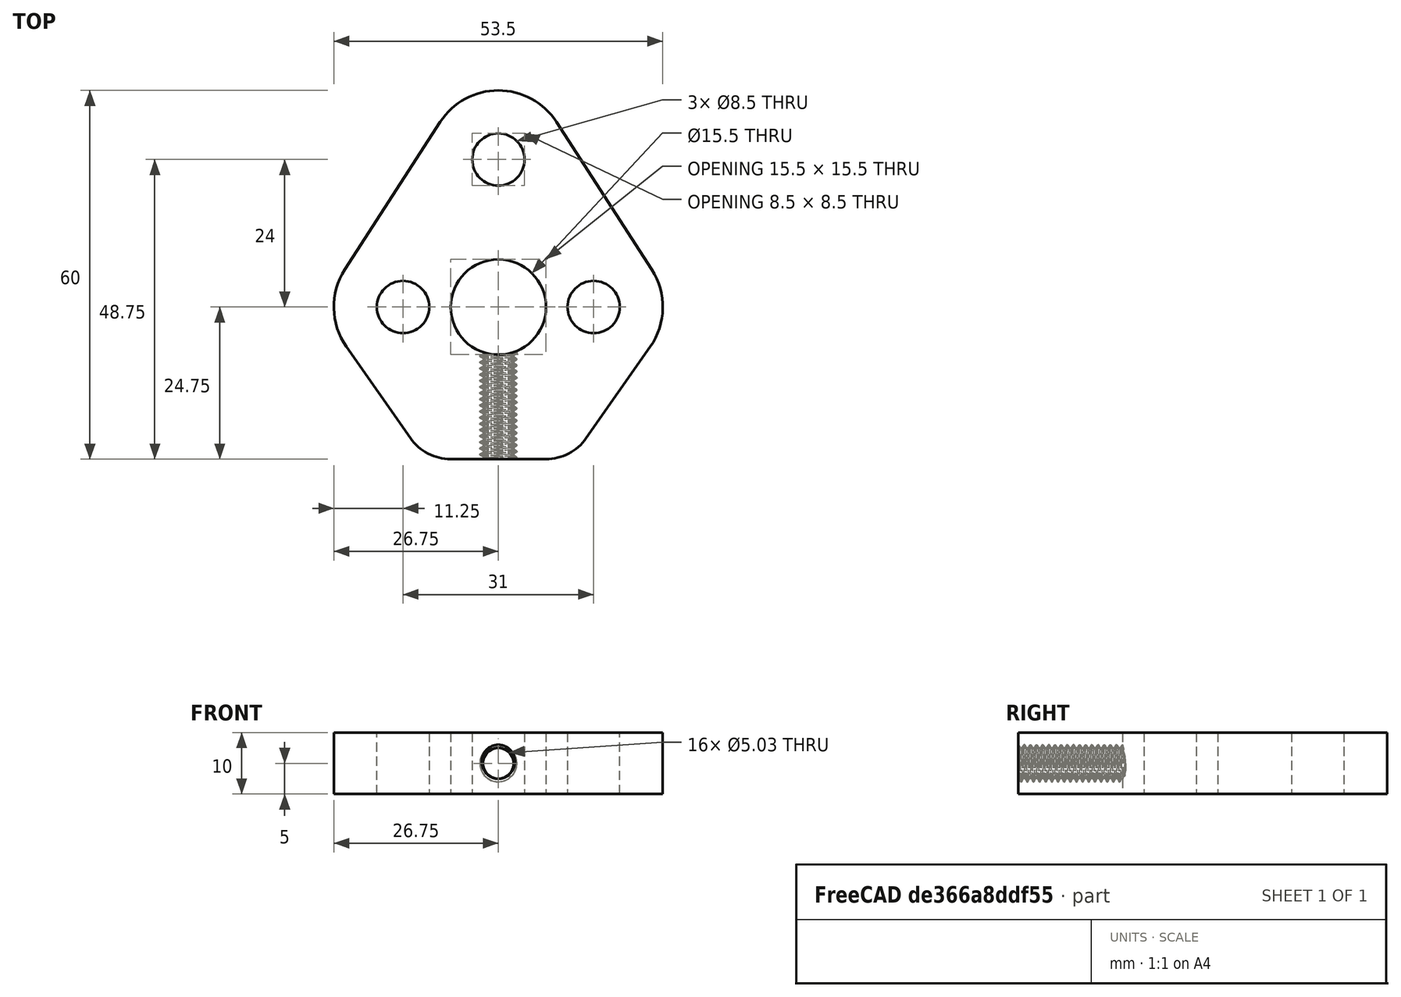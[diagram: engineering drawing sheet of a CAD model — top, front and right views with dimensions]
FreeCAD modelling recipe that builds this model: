
FCSTD DOCUMENT  (FreeCAD 0.20R29177 (Git))
Label: Поворот сортировщика семян
License: All rights reserved
LicenseURL: http://en.wikipedia.org/wiki/All_rights_reserved
objects: TechDraw::DrawProjGroupItem×4, Sketcher::SketchObject×2, TechDraw::DrawViewBalloon×2, TechDraw::DrawViewDimension×2, Mesh::Feature×1, PartDesign::Pad×1, PartDesign::Mirrored×1, TechDraw::DrawSVGTemplate×1, PartDesign::Hole×1, PartDesign::Body×1, TechDraw::DrawProjGroup×1, TechDraw::DrawPage×1
note: 8 computed .brp shape members not serialized (recipe doc carries the construction recipe); baked Part::Feature solids carry a one-line shape summary decoded from their .brp

FEATURE [Mesh::Feature] __________________________________________________2  label="поворот сортировщика семян2"
FEATURE [Sketcher::SketchObject] Sketch
  FullyConstrained = true
  MapMode = 5
  Support = -> [XY_Plane]
  sketch-geometry (12):
    g0: Circle CenterX=15.5 CenterY=0 CenterZ=0 NormalX=0 NormalY=0 NormalZ=1 AngleXU=0 Radius=4.25
    g1: ArcOfCircle CenterX=0 CenterY=0 CenterZ=0 NormalX=0 NormalY=0 NormalZ=1 AngleXU=0 Radius=7.75 StartAngle=4.71239 EndAngle=7.85398
    g2: ArcOfCircle CenterX=0 CenterY=24 CenterZ=0 NormalX=0 NormalY=0 NormalZ=1 AngleXU=0 Radius=4.25 StartAngle=4.71239 EndAngle=7.85398
    g3: ArcOfCircle CenterX=0 CenterY=24 CenterZ=0 NormalX=0 NormalY=0 NormalZ=1 AngleXU=0 Radius=11.25 StartAngle=0.573441 EndAngle=1.5708
    g4: ArcOfCircle CenterX=15.5 CenterY=0 CenterZ=0 NormalX=0 NormalY=0 NormalZ=1 AngleXU=0 Radius=11.25 StartAngle=5.67281 EndAngle=6.85663
    g5: ArcOfCircle CenterX=7.75 CenterY=-16.75 CenterZ=0 NormalX=0 NormalY=0 NormalZ=1 AngleXU=0 Radius=8 StartAngle=4.71239 EndAngle=5.67281
    g6: LineSegment StartX=7.75 StartY=-24.75 StartZ=0 EndX=0 EndY=-24.75 EndZ=0
    g7: LineSegment StartX=14.3055 StartY=-21.3354 StartZ=0 EndX=24.7187 EndY=-6.44818 EndZ=0
    g8: LineSegment StartX=0 StartY=-24.75 StartZ=0 EndX=-1.4e-15 EndY=-7.75 EndZ=0
    g9: LineSegment StartX=2.4e-15 StartY=7.75 StartZ=0 EndX=-8e-16 EndY=19.75 EndZ=0
    g10: LineSegment StartX=1.3e-15 StartY=28.25 StartZ=0 EndX=7e-16 EndY=35.25 EndZ=0
    g11: LineSegment StartX=9.45044 StartY=30.1034 StartZ=0 EndX=24.9504 EndY=6.10341 EndZ=0
  constraints (38):
    c: PointOnObject(g0,g-1)
    c: Coincident(g1,g-1)
    c: PointOnObject(g1,g-2)
    c: PointOnObject(g1,g-2)
    c: PointOnObject(g2,g-2)
    c: PointOnObject(g2,g-2)
    c: PointOnObject(g2,g-2)
    c: Coincident(g3,g2)
    c: PointOnObject(g3,g-2)
    c: Coincident(g4,g0)
    c: Coincident(g6,g5)
    c: PointOnObject(g6,g-2)
    c: Horizontal(g6)
    c: Coincident(g7,g5)
    c: Coincident(g7,g4)
    c: Coincident(g8,g6)
    c: Coincident(g8,g1)
    c: Coincident(g9,g1)
    c: Coincident(g9,g2)
    c: Coincident(g10,g2)
    c: Coincident(g10,g3)
    c: Coincident(g11,g3)
    c: Coincident(g11,g4)
    c: Diameter(g0) = 8.5
    c: Diameter(g2) = 8.5
    c: Diameter(g1) = 15.5
    c: DistanceX(g0) = 15.5
    c: DistanceY(g2) = 24
    c: Diameter(g4) = 22.5
    c: Equal(g3,g4)
    c: Tangent(g4,g11)
    c: Tangent(g11,g3)
    c: Tangent(g4,g7)
    c: Tangent(g6,g5)
    c: Tangent(g5,g7)
    c: Distance(g8) = 17
    c: Diameter(g5) = 16
    c: DistanceX(g5) = 7.75
FEATURE [PartDesign::Pad] Pad
  Direction = (0,0,1)
  Length = 10
  Length2 = 100
  Midplane = true
  Profile = -> Sketch
  Type = 0
FEATURE [PartDesign::Mirrored] Mirrored
  BaseFeature = -> Pad
  MirrorPlane = -> Sketch [V_Axis]
  Originals = -> [Pad]
FEATURE [TechDraw::DrawSVGTemplate] Template
  EditableTexts = AUTHOR_NAME=AUTHOR NAME; DN=DN; DRAWING_TITLE=DRAWING TITLE; FC-DATE=DD/MM/YYYY; FC-REV=REV A; FC-SC=SCALE; FC-SH=X / Y; FC-SI=A4; FreeCAD_DRAWING=FreeCAD DRAWING; PN=PN
  Height = 210
  Orientation = 1
  Width = 297
FEATURE [Sketcher::SketchObject] Sketch001
  FullyConstrained = true
  MapMode = 5
  Placement = pos=(0,0,0) rot=(1,0,0;1.5708rad)
  Support = -> [XZ_Plane]
  sketch-geometry (1):
    g0: Circle CenterX=0 CenterY=0 CenterZ=0 NormalX=0 NormalY=0 NormalZ=1 AngleXU=0 Radius=3
  constraints (2):
    c: Coincident(g0,g-1)
    c: Diameter(g0) = 6
FEATURE [PartDesign::Hole] Hole
  BaseFeature = -> Mirrored
  CustomThreadClearance = 0
  Depth = 163.486
  DepthType = 1
  Diameter = 5.026
  DrillForDepth = false
  DrillPoint = 1
  DrillPointAngle = 118
  HoleCutCountersinkAngle = 90
  HoleCutCustomValues = false
  HoleCutDepth = 6.4
  HoleCutDiameter = 13.4
  HoleCutType = 2
  ModelThread = true
  Profile = -> Sketch001
  Refine = true
  Reversed = true
  Tapered = false
  TaperedAngle = 90
  ThreadClass = 0
  ThreadDepth = 163.486
  ThreadDepthType = 0
  ThreadDirection = 0
  ThreadFit = 0
  ThreadSize = 14
  ThreadType = 1
  Threaded = true
  UseCustomThreadClearance = false
FEATURE [PartDesign::Body] Body
  Group = -> [Sketch,Pad,Mirrored,Sketch001,Hole]
  Origin = -> Origin
  Tip = -> Hole
FEATURE [TechDraw::DrawProjGroupItem] ProjItem  label="Front"
  CoarseView = false
  Direction = (0,0,-1)
  Focus = 100
  HardHidden = false
  IsoCount = 0
  IsoHidden = false
  IsoVisible = false
  LockPosition = true
  Perspective = false
  Rotation = 0
  RotationVector = (1,0,0)
  ScaleType = 2
  SeamHidden = false
  SeamVisible = true
  SmoothHidden = false
  SmoothVisible = true
  Source = -> [Body]
  Type = 0
  X = 0
  XDirection = (1,0,0)
  Y = 0
FEATURE [TechDraw::DrawProjGroupItem] ProjItem003  label="Top"
  CoarseView = false
  Direction = (0,-1,0)
  Focus = 100
  HardHidden = false
  IsoCount = 0
  IsoHidden = false
  IsoVisible = false
  LockPosition = false
  Perspective = false
  Rotation = 0
  RotationVector = (1,0,0)
  ScaleType = 2
  SeamHidden = false
  SeamVisible = true
  SmoothHidden = false
  SmoothVisible = true
  Source = -> [Body]
  Type = 4
  X = 0
  XDirection = (1,0,0)
  Y = -100
FEATURE [TechDraw::DrawProjGroupItem] ProjItem004  label="Left"
  CoarseView = false
  Direction = (-1,0,-1e-16)
  Focus = 100
  HardHidden = false
  IsoCount = 0
  IsoHidden = false
  IsoVisible = false
  LockPosition = false
  Perspective = false
  Rotation = 0
  RotationVector = (1,0,0)
  ScaleType = 2
  SeamHidden = false
  SeamVisible = true
  SmoothHidden = false
  SmoothVisible = true
  Source = -> [Body]
  Type = 1
  X = 50
  XDirection = (1e-16,0,-1)
  Y = 0
FEATURE [TechDraw::DrawProjGroupItem] ProjItem005  label="FrontTopLeft"
  CoarseView = false
  Direction = (-0.57735,-0.57735,-0.57735)
  Focus = 100
  HardHidden = false
  IsoCount = 0
  IsoHidden = false
  IsoVisible = false
  LockPosition = false
  Perspective = false
  Rotation = 0
  RotationVector = (1,0,0)
  ScaleType = 2
  SeamHidden = false
  SeamVisible = true
  SmoothHidden = false
  SmoothVisible = true
  Source = -> [Body]
  Type = 6
  X = 67.4506
  XDirection = (0.707107,0,-0.707107)
  Y = -75.9441
FEATURE [TechDraw::DrawProjGroup] ProjGroup
  Anchor = -> ProjItem
  AutoDistribute = true
  LockPosition = false
  ProjectionType = 0
  Rotation = 0
  ScaleType = 2
  Source = -> [Body]
  Views = -> [ProjItem,ProjItem003,ProjItem004,ProjItem005]
  X = 50.5405
  Y = 149.549
  spacingX = 15
  spacingY = 15
FEATURE [TechDraw::DrawViewBalloon] Balloon
  BubbleShape = 0
  EndType = 0
  EndTypeScale = 1
  KinkLength = 5
  LockPosition = false
  OriginX = 17.7044
  OriginY = 8.56843
  Rotation = 0
  ScaleType = 0
  ShapeScale = 1
  SourceView = -> ProjItem
  Text = M8
  TextWrapLen = -1
  X = 37.7044
  Y = 28.5684
FEATURE [TechDraw::DrawViewBalloon] Balloon001
  BubbleShape = 0
  EndType = 0
  EndTypeScale = 1
  KinkLength = 5
  LockPosition = false
  OriginX = -1.83659
  OriginY = 2.48537
  Rotation = 0
  ScaleType = 0
  ShapeScale = 1
  SourceView = -> ProjItem003
  Text = M6
  TextWrapLen = -1
  X = 18.1634
  Y = 22.4854
FEATURE [TechDraw::DrawViewDimension] Dimension
  AngleOverride = false
  Arbitrary = false
  ArbitraryTolerances = false
  EqualTolerance = true
  ExtensionAngle = 0
  FormatSpec = %.2f
  FormatSpecOverTolerance = %+.2f
  FormatSpecUnderTolerance = %+.2f
  Inverted = false
  LineAngle = 0
  LockPosition = false
  MeasureType = 1
  OverTolerance = 0
  References2D = -> [ProjItem]
  Rotation = 0
  ScaleType = 0
  TheoreticalExact = false
  Type = 1
  UnderTolerance = 0
  X = 7.28612
  Y = 20.3261
FEATURE [TechDraw::DrawViewDimension] Dimension001
  AngleOverride = false
  Arbitrary = false
  ArbitraryTolerances = false
  EqualTolerance = true
  ExtensionAngle = 0
  FormatSpec = %.2f
  FormatSpecOverTolerance = %+.2f
  FormatSpecUnderTolerance = %+.2f
  Inverted = false
  LineAngle = 0
  LockPosition = false
  MeasureType = 1
  OverTolerance = 0
  References2D = -> [ProjItem]
  Rotation = 0
  ScaleType = 0
  TheoreticalExact = false
  Type = 2
  UnderTolerance = 0
  X = -33.6313
  Y = -6.75
FEATURE [TechDraw::DrawPage] Page
  KeepUpdated = true
  NextBalloonIndex = 6
  ProjectionType = 0
  Template = -> Template
  Views = -> [ProjGroup,Balloon,Balloon001,Dimension,Dimension001]
